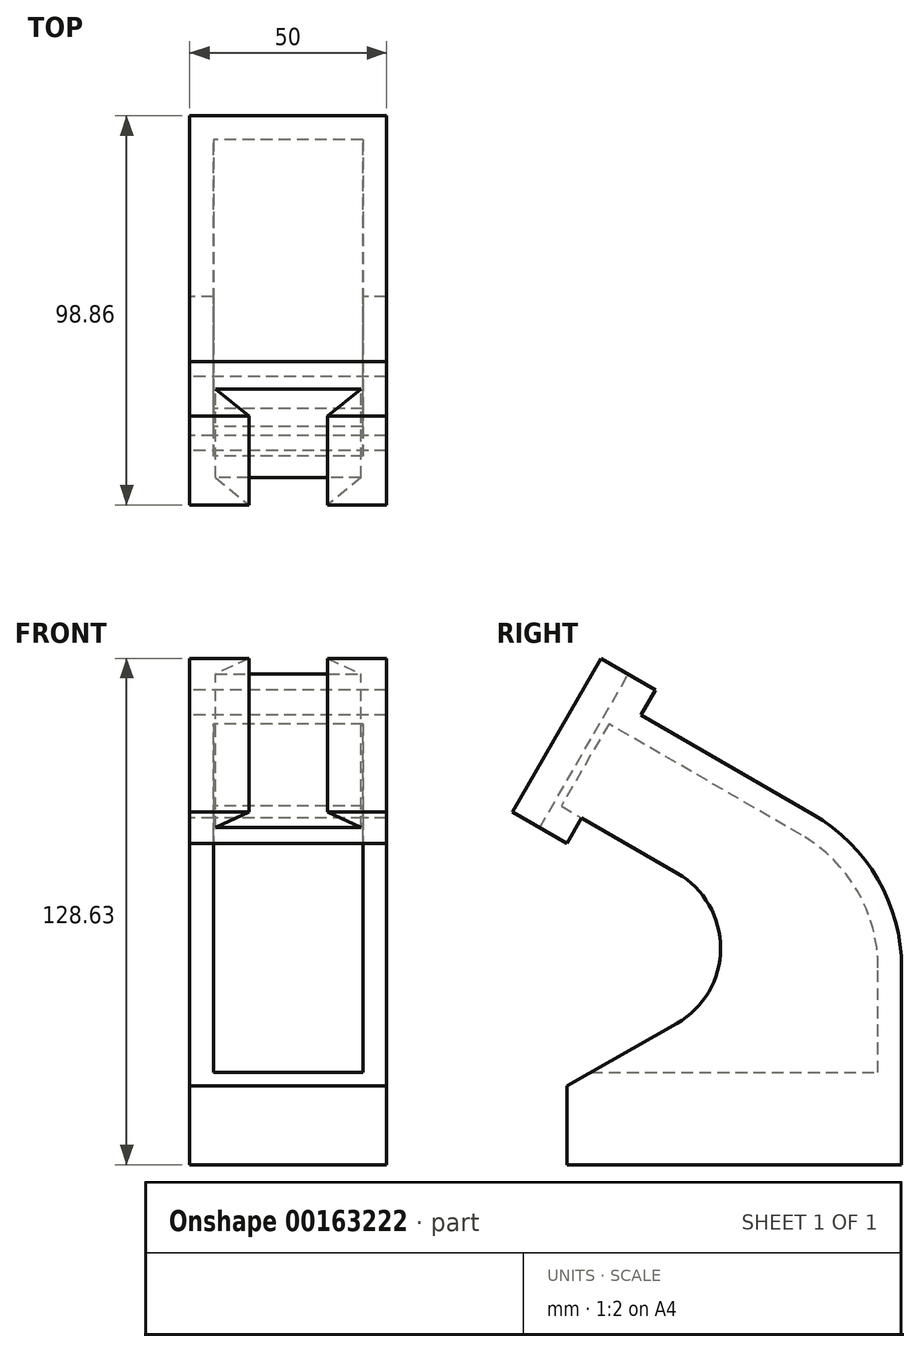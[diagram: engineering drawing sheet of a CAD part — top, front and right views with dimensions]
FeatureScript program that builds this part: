
annotation { "Feature Type Name" : "Feature", "Feature Type Description" : "" }
export const myFeature = defineFeature(function(context is Context, id is Id, definition is map)
    precondition{}
    {
        {
            var Q0;
            Q0=qCreatedBy(makeId("Right.planeOp"),FACE);
            var sketch = newSketch(context, id + "F0", { "sketchPlane" : qUnion([Q0])});
            skLineSegment(sketch, "E0", {"start": v(0, 0) * mm, "end": v(85, 0) * mm});
            skLineSegment(sketch, "E1", {"start": v(85, 0) * mm, "end": v(85, 50) * mm});
            skLineSegment(sketch, "E2", {"start": v(0, 0) * mm, "end": v(0, 20) * mm});
            skLineSegment(sketch, "E3", {"start": v(0, 20) * mm, "end": v(27.89, 35.88) * mm});
            skLineSegment(sketch, "E4", {"start": v(62.5, 88.97) * mm, "end": v(18.8, 114.2) * mm});
            skLineSegment(sketch, "E5", {"start": v(18.8, 114.2) * mm, "end": v(22.5, 120.63) * mm});
            skLineSegment(sketch, "E6", {"start": v(22.5, 120.63) * mm, "end": v(8.64, 128.63) * mm});
            skLineSegment(sketch, "E7", {"start": v(8.64, 128.63) * mm, "end": v(-13.86, 89.66) * mm});
            skLineSegment(sketch, "E8", {"start": v(-13.86, 89.66) * mm, "end": v(0, 81.66) * mm});
            skLineSegment(sketch, "E9", {"start": v(0, 81.66) * mm, "end": v(3.7, 88.08) * mm});
            skLineSegment(sketch, "E10", {"start": v(3.7, 88.08) * mm, "end": v(28, 74.05) * mm});
            skArc(sketch, "E11", {"start": v(62.5, 88.97) * mm, "mid": v(78.97, 72.5) * mm, "end": v(85, 50) * mm});
            skArc(sketch, "E12", {"start": v(27.89, 35.88) * mm, "mid": v(39, 54.94) * mm, "end": v(28, 74.05) * mm});
            skLineSegment(sketch, "E13", {"start": v(0, 81.66) * mm, "end": v(18.8, 114.2) * mm, "construction": true});
            skPoint(sketch, "E14", {"position": v(-2.6, 109.14) * mm});
            skLineSegment(sketch, "E15", {"start": v(-2.6, 109.14) * mm, "end": v(11.46, 101.02) * mm, "construction": true});
            skSolve(sketch);
        }
        {
            var Q0;
            Q0 = qSketchRegion(id + "F0", true);
            extrude(context, id + "F1", {"entities" : qUnion([Q0]), "endBound" : BoundingType.SYMMETRIC, "depth" : 50 * mm, "hasSecondDirection" : true, "secondDirectionOppositeDirection" : true, "secondDirectionDepth" : 50 * mm});
        }
        {
            var Q0;
            Q0=makeQuery(id+"F1.opExtrude","SWEPT_FACE",FACE,{"disambiguationData":[OSD([sQuery(id+"F0.wireOp",EDGE,"E10")])]});
            var Q1;
            Q1=makeQuery(id+"F1.opExtrude","SWEPT_FACE",FACE,{"disambiguationData":[OSD([sQuery(id+"F0.wireOp",EDGE,"E12")])]});
            var Q2;
            Q2=makeQuery(id+"F1.opExtrude","SWEPT_FACE",FACE,{"disambiguationData":[OSD([sQuery(id+"F0.wireOp",EDGE,"E3")])]});
            shell(context, id + "F2", {"entities" : qUnion([Q0, Q1, Q2]), "thickness" : 6 * mm});
        }
        {
            var Q0;
            Q0=makeQuery(id+"F2.opShell","OFFSET_FACE",FACE,{"disambiguationData":[OSD([sQuery(id+"F0.wireOp",EDGE,"E7")])]});
            extrude(context, id + "F3", {"entities" : qUnion([Q0]), "operationType" : NewBodyOperationType.ADD, "depth" : 4 * mm});
        }
        {
            var Q0;
            Q0=makeQuery(id+"F1.opExtrude","SWEPT_FACE",FACE,{"disambiguationData":[OSD([sQuery(id+"F0.wireOp",EDGE,"E6")])]});
            var sketch = newSketch(context, id + "F4", { "sketchPlane" : qUnion([Q0])});
            skLineSegment(sketch, "E16.bottom", {"start": v(-10, -56.83) * mm, "end": v(10, -56.83) * mm});
            skLineSegment(sketch, "E16.top", {"start": v(-18.5, -48.83) * mm, "end": v(18.5, -48.83) * mm});
            skLineSegment(sketch, "E16.left", {"start": v(-10, -56.83) * mm, "end": v(-18.5, -48.83) * mm});
            skLineSegment(sketch, "E16.right", {"start": v(10, -56.83) * mm, "end": v(18.5, -48.83) * mm});
            skPoint(sketch, "E17", {"position": v(0, -48.83) * mm});
            skPoint(sketch, "E18", {"position": v(0, -56.83) * mm});
            skLineSegment(sketch, "E19", {"start": v(0, -48.83) * mm, "end": v(0, -64.83) * mm, "construction": true});
            skSolve(sketch);
        }
        {
            var Q0;
            Q0=makeQuery(id+"F4.imprint","IMPRINT",FACE,{"disambiguationData":[TD([[makeQuery(id+"F4.imprint","IMPRINT",EDGE,{"derivedFrom":sQuery(id+"F4.wireOp",EDGE,"E16.bottom")}),-1.0]])]});
            extrude(context, id + "F5", {"entities" : qUnion([Q0]), "operationType" : NewBodyOperationType.REMOVE, "endBound" : BoundingType.UP_TO_NEXT, "oppositeDirection" : true, "depth" : 25 * mm});
        }
        {
            var Q0;
            Q0=makeQuery(id+"F2.opShell","OFFSET_FACE",FACE,{"disambiguationData":[OSD([sQuery(id+"F0.wireOp",EDGE,"E0")])]});
            var Q1;
            {var subQ0=sQuery(id+"F0.wireOp",EDGE,"E3");var subQ1=sQuery(id+"F0.wireOp",EDGE,"E2");Q1=makeQuery(id+"F2.opShell","OFFSET_VERTEX",VERTEX,{"disambiguationData":[OSD([subQ1,subQ0]),TDD([makeQuery(id+"F1.opExtrude","CAP_VERTEX",VERTEX,{"disambiguationData":[OSD([subQ1,subQ0])],"isStart":true})])]});}
            extrude(context, id + "F6", {"entities" : qUnion([Q0]), "operationType" : NewBodyOperationType.ADD, "endBound" : BoundingType.UP_TO_VERTEX, "endBoundEntityVertex" : qUnion([Q1]), "depth" : 25 * mm});
        }
    });
